# Revit family: KJU-ACDI-DAFWSxxx
name_source: partatom
category: Leuchten
units: mm (PartAtom-declared; Revit-internal decimal feet)

## family parameters
Basisbauteil = Fläche
Beim Laden mit Abzugskörper schneiden = Nein
Bemaßung runder Anschluss = Durchmesser verwenden
Gemeinsam genutzt = Nein
Lichtquelle = Ja
OmniClass-Nummer = 23.80.70.11
OmniClass-Titel = Luminaries for Internal Lighting
Raumberechnungspunkt = Nein
Teiletyp = Normal

## types (4) — shared parameters
Baugruppenkennzeichen = D5020200
Emissionsform beim Rendern sichtbar = Nein
Farbfilter = 16777215
Farbtemperaturverschiebung bei Dämpfen der Lampe = <Keine Auswahl>
Hersteller = RIDI Leuchten GmbH
Lampe = LED
Neigungswinkel = 90.00°
Scheinlast = 25 VA
URL = www.spectral.de
Von Kreisdurchmesser aussenden = 293 mm
brand = Spectral
conformity mark = CE
electrical safety class = 1
height = 51 mm
ingress protection (IP) code = IP20
length = 293 mm
nominal frequency = 50-60Hz
nominal voltage = 230
rated input power = 25
voltage type (AC, DC, UC) = AC
weight = 1,9 kg
width = 293 mm
zero-valued in all types: Vorgabe-Ansicht

## per-type parameters (varying)
| type | Datei für fotometrisches Netz | Modell |
| KJU-ACDI DAFWS830APS0300 | KJU-xCDI xxxAPSxx.IES | SPG0630194AH |
| KJU-ACDI DAFWS830OS0300 | KJU-xCDI xxxOSxx.IES | SPG0630196AH |
| KJU-ACDI DAFWS840APS0300 | KJU-xCDI xxxAPSxx.IES | SPG0630197AH |
| KJU-ACDI DAFWS840OS0300 | KJU-xCDI xxxOSxx.IES | SPG0630199AH |

note: column(s) folded — value = type name in every type: product name
